# Revit family: Building-IEC309Connections-GEWISS-66IB-INTERLOCKED-SOCKET-OUTLETS-HD_IP66_125A_RCBO
name_source: partatom
category: Apparecchi elettrici
revit_build: Autodesk Revit 2016 (Build: 20161004_0715(x64)
units: mm (PartAtom-declared; Revit-internal decimal feet)

## family parameters
Condiviso = No
Host = Muro
Mantenere orientamento annotazione = Sì
Numero OmniClass = 23.80.50.14
Punto di calcolo locali = No
Quota connettore circolare = Usa diametro
Sempre verticale = Sì
Taglio con vuoti quando caricato = No
Tipo di parte = Normale
Titolo OmniClass = Plug Connectors

## types (1)
- Building-IEC309Connections-GEWISS-66IB-INTERLOCKED-SOCKET-OUTLETS-HD_IP66_125A_RCBO
    Carico apparente = 0 VA
    Catalogue = BUILDING
    Catalogue Range = 66 IB
    Circuit breaker = 125A 25 kA C characteristic 30-3000 mA
    Classificazione carico = Altro
    Colour = Black
    Colour: = Black
    Descrizione = SOCKET I.W.B.3P+N+E  125A 500V 7H IP55-D
    EAN code = 8011564110175
    Electrocod = 2221
    Frequency = 50/60 Hz
    Glow Wire Test = 850 °C (Socket) - 960 °C (Case)
    Glow wire test: = 850 °C (Socket) - 960 °C (Case)
    H_da terra = 1000 mm  [stored 3.28084 ft]
    IDF = cf41bd39-93ee-4b38-ab27-d721bae31115
    IDT = f718bfbe-2e95-47eb-9ef0-79672bd4d97c
    IP degree = IP55
    Immagine tipo = GW66597.jpg
    Impact resistance at -20 °C = 20J
    Modello = GW66598
    No. of poles = 3P+N+E
    Number of poles = 3P+N+E
    Numero poli = 3
    Operating temperature: = -25 +40 °C
    Pomello = <Per categoria>
    Pomello basso = <Per categoria>
    Potenza = 500 V
    Presa = GEWISS - NERO
    Produttore = GEWISS S.p.A.
    Protection = MCB+ADD-ON RCD
    Rated current (A) = 125
    Rated current (In) = 125
    Rated frequency (Hz) = 50/60 Hz
    Rated voltage = 480-500V
    Reference h = 7
    SEO = Socket outlet
    Shock resistance = IK10
    Struttura = GEWISS - Grigio RAL - 7035
    Technical sheet = https://www.gewiss.com
    Terminal tightening capacity = 2,5-50 mm² flexible cables - 2,5-70 mm² rigid cables
    Thermo-pressure with ball = 200
    Tipo simbolo = PRESAINDSTAGNA : 3P
    Type of use = Heavy duty
    Typology = Vertical
    URL = https://www.gewiss.com
    Version file RFA = 18.0
    Working temperature = -25 ÷ +40 °C

note: source unit labels omitted for Thermo-pressure with ball — the stored unit's dimension contradicts the parameter name (converter mislabeling)

note: [stored X ft] marks values corroborated as IEEE doubles in the binary element streams (Revit-internal decimal feet)

## geometry (parser evidence)
native form markers: Blend x2, Sweep x2
no freeform markers — native parametric forms only
